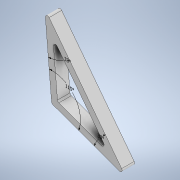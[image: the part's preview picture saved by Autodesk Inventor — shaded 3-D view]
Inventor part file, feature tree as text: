
AUTODESK INVENTOR PART (.ipt)
format: ipt  version: 2021.1 (Build 251245000, 245)  size: 135,168 bytes
history: native  units: in
note: dims shown in document units (in); Inventor stores cm internally (conversion verified against a paired STEP export)
features: other x4, extrude x2, fillet x2
ambient origin geometry x8: Origin, YZ Plane, XZ Plane, XY Plane, X Axis, Y Axis, Z Axis, Center Point
bodies: Solid1 (feature_tree)
feature tree (8):
  other  "Annotations"
  extrude  "Extrusion1"  Depth=0.75in TaperAngle=0.0deg
  extrude  "Extrusion2"  Depth=0.375in
  fillet  "Fillet1"  Radius=0.375in
  fillet  "Fillet2"  Radius=0.375in
  other  "Angular Dimension 1"
  other  "Angular Dimension 3"
  other  "Angular Dimension 4"
